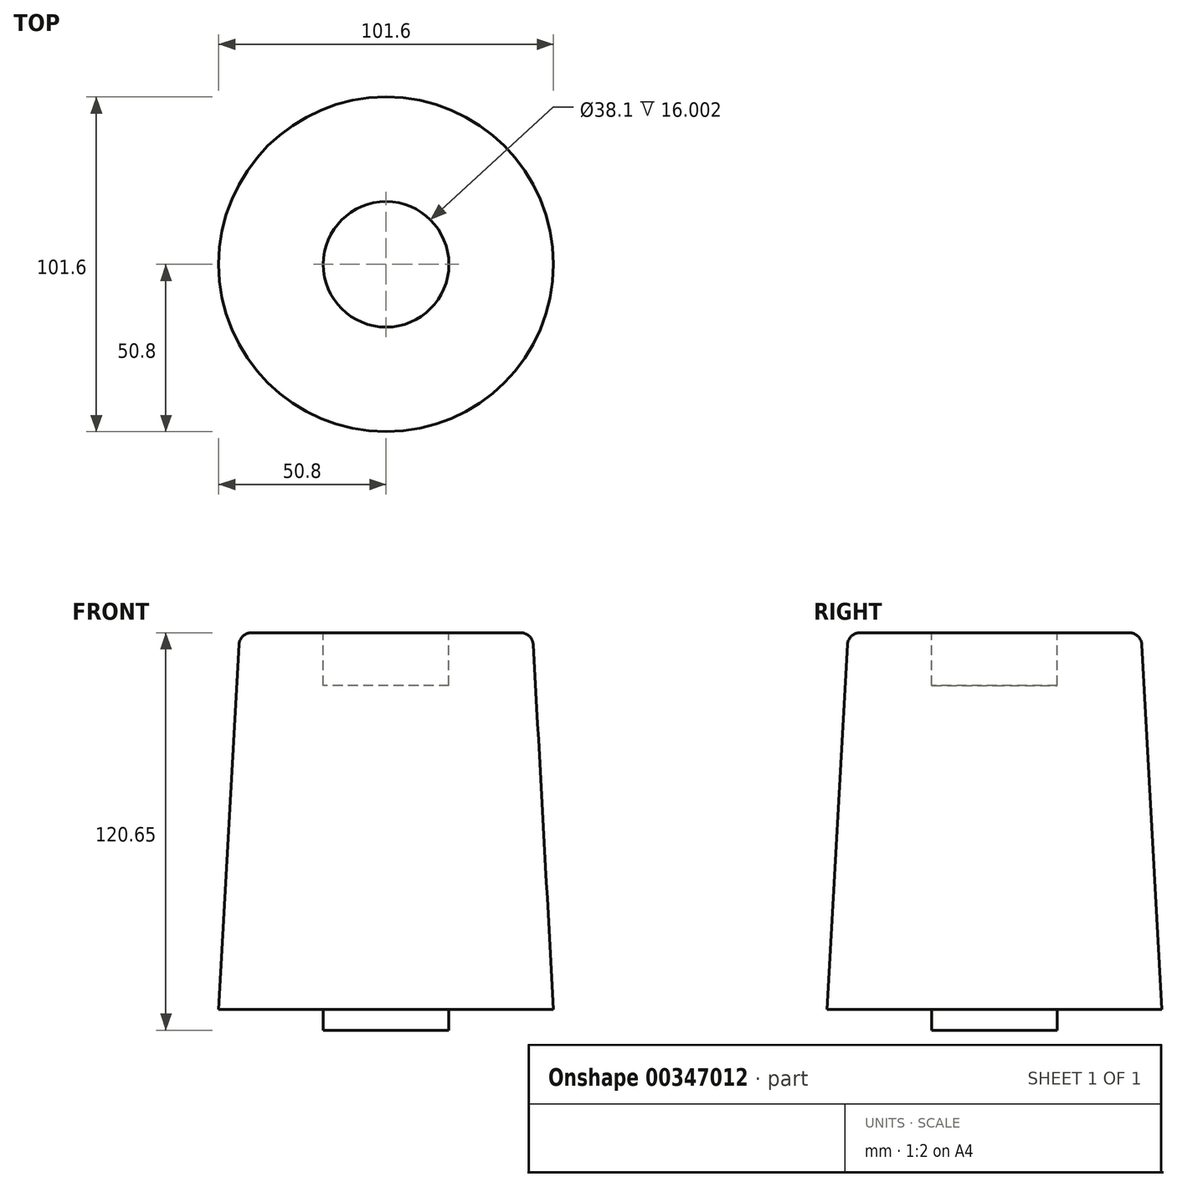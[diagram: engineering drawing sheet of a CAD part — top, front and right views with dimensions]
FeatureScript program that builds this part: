
annotation { "Feature Type Name" : "Feature", "Feature Type Description" : "" }
export const myFeature = defineFeature(function(context is Context, id is Id, definition is map)
    precondition{}
    {
        {
            var Q0;
            Q0=qCreatedBy(makeId("Front.planeOp"),FACE);
            var sketch = newSketch(context, id + "F0", { "sketchPlane" : qUnion([Q0])});
            skLineSegment(sketch, "E0", {"start": v(0, 60.97) * mm, "end": v(0, -53.33) * mm});
            skLineSegment(sketch, "E1", {"start": v(0, -53.33) * mm, "end": v(-50.8, -53.33) * mm});
            skLineSegment(sketch, "E2", {"start": v(-50.8, -53.33) * mm, "end": v(-44.65, 57.37) * mm});
            skLineSegment(sketch, "E3", {"start": v(-40.85, 60.97) * mm, "end": v(0, 60.97) * mm});
            skPoint(sketch, "E4.visualSharp", {"position": v(-44.45, 60.97) * mm});
            skArc(sketch, "E4.filletArc", {"start": v(-40.85, 60.97) * mm, "mid": v(-43.46, 59.93) * mm, "end": v(-44.65, 57.37) * mm});
            skSolve(sketch);
        }
        {
            var Q0;
            Q0 = qSketchRegion(id + "F0", true);
            var Q1;
            Q1=sQuery(id+"F0.wireOp",EDGE,"E0");
            revolve(context, id + "F1", {"entities" : qUnion([Q0]), "axis" : qUnion([Q1]), "revolveType" : RevolveType.FULL});
        }
        {
            var Q0;
            Q0=makeQuery(id+"F1.opRevolve","SWEPT_FACE",FACE,{"disambiguationData":[OSD([sQuery(id+"F0.wireOp",EDGE,"E1")])]});
            var sketch = newSketch(context, id + "F2", { "sketchPlane" : qUnion([Q0])});
            skCircle(sketch, "E5", {"center": v(0, 0) * mm, "radius": 19.05 * mm});
            skSolve(sketch);
        }
        {
            var Q0;
            Q0=makeQuery(id+"F2.imprint","IMPRINT",FACE,{"disambiguationData":[TD([[makeQuery(id+"F2.imprint","IMPRINT",EDGE,{"derivedFrom":sQuery(id+"F2.wireOp",EDGE,"E5")}),1.0]])]});
            extrude(context, id + "F3", {"entities" : qUnion([Q0]), "operationType" : NewBodyOperationType.ADD, "depth" : 6.35 * mm});
        }
        {
            var Q0;
            Q0=makeQuery(id+"F1.opRevolve","SWEPT_FACE",FACE,{"disambiguationData":[OSD([sQuery(id+"F0.wireOp",EDGE,"E3")])]});
            var sketch = newSketch(context, id + "F4", { "sketchPlane" : qUnion([Q0])});
            skCircle(sketch, "E6", {"center": v(0, 0) * mm, "radius": 19.05 * mm});
            skSolve(sketch);
        }
        {
            var Q0;
            Q0=makeQuery(id+"F4.imprint","IMPRINT",FACE,{"disambiguationData":[TD([[makeQuery(id+"F4.imprint","IMPRINT",EDGE,{"derivedFrom":sQuery(id+"F4.wireOp",EDGE,"E6")}),1.0]])]});
            extrude(context, id + "F5", {"entities" : qUnion([Q0]), "operationType" : NewBodyOperationType.REMOVE, "oppositeDirection" : true, "depth" : 16 * mm});
        }
    });
